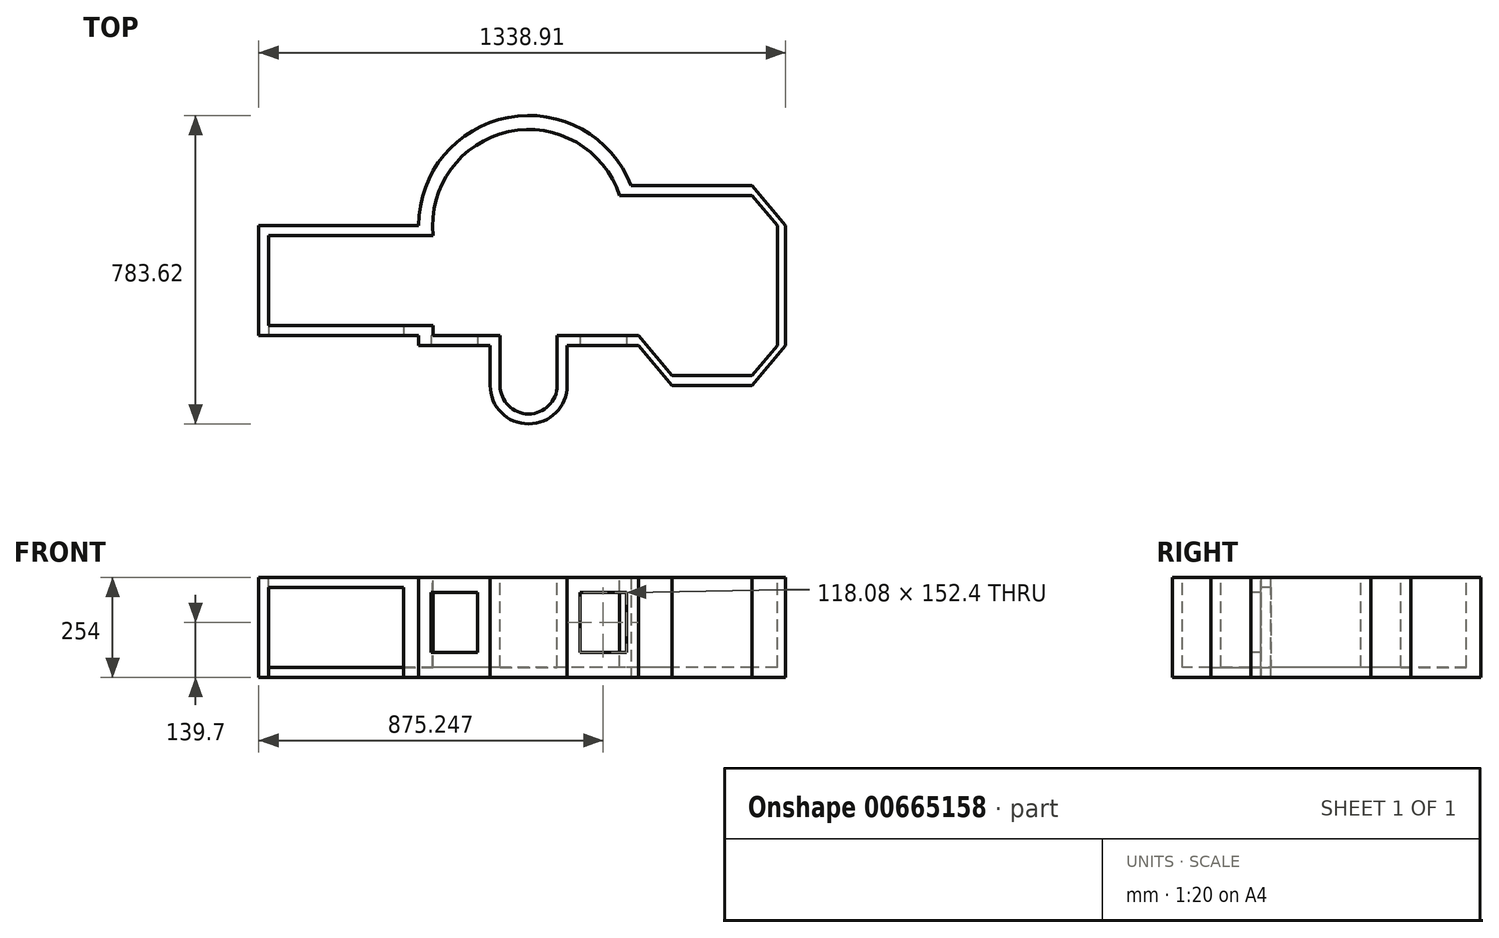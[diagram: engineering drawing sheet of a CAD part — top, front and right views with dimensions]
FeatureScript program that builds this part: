
annotation { "Feature Type Name" : "Feature", "Feature Type Description" : "" }
export const myFeature = defineFeature(function(context is Context, id is Id, definition is map)
    precondition{}
    {
        {
            var Q0;
            Q0=qCreatedBy(makeId("Top.planeOp"),FACE);
            var sketch = newSketch(context, id + "F0", { "sketchPlane" : qUnion([Q0])});
            skLineSegment(sketch, "E0.bottom", {"start": v(279.4, -152.4) * mm, "end": v(97.82, -152.4) * mm});
            skLineSegment(sketch, "E0.right", {"start": v(-279.4, -152.4) * mm, "end": v(-279.4, -127) * mm});
            skPoint(sketch, "E0.middle", {"position": v(0, 0) * mm});
            skLineSegment(sketch, "E1.0", {"start": v(-97.82, -152.4) * mm, "end": v(-97.82, -254) * mm});
            skLineSegment(sketch, "E2.0", {"start": v(97.82, -152.4) * mm, "end": v(97.82, -254) * mm});
            skLineSegment(sketch, "E3", {"start": v(-279.4, 152.4) * mm, "end": v(-685.8, 152.4) * mm});
            skLineSegment(sketch, "E4", {"start": v(-685.8, 152.4) * mm, "end": v(-685.8, -127) * mm});
            skLineSegment(sketch, "E5", {"start": v(-685.8, -127) * mm, "end": v(-279.4, -127) * mm});
            skLineSegment(sketch, "E6", {"start": v(567.85, 254) * mm, "end": v(653.1, 152.4) * mm});
            skLineSegment(sketch, "E7", {"start": v(653.1, 152.4) * mm, "end": v(653.1, -152.4) * mm});
            skLineSegment(sketch, "E8", {"start": v(653.1, -152.4) * mm, "end": v(567.85, -254) * mm});
            skLineSegment(sketch, "E9", {"start": v(567.85, -254) * mm, "end": v(364.65, -254) * mm});
            skLineSegment(sketch, "E10", {"start": v(364.65, -254) * mm, "end": v(279.4, -152.4) * mm});
            skArc(sketch, "E11", {"start": v(-97.82, -254) * mm, "mid": v(0, -351.82) * mm, "end": v(97.82, -254) * mm});
            skLineSegment(sketch, "E12.trimOffspring", {"start": v(-97.82, -152.4) * mm, "end": v(-279.4, -152.4) * mm});
            skArc(sketch, "E13", {"start": v(260.27, 254) * mm, "mid": v(-51.7, 426.98) * mm, "end": v(-279.4, 152.4) * mm});
            skLineSegment(sketch, "E14", {"start": v(567.85, 254) * mm, "end": v(260.27, 254) * mm});
            skSolve(sketch);
        }
        {
            var Q0;
            Q0=makeQuery(id+"F0.imprint","IMPRINT",FACE,{"disambiguationData":[TD([[makeQuery(id+"F0.imprint","IMPRINT",EDGE,{"derivedFrom":sQuery(id+"F0.wireOp",EDGE,"E0.bottom")}),-1.0]])]});
            extrude(context, id + "F1", {"entities" : qUnion([Q0]), "depth" : 254 * mm, "offsetDistance" : 25.4 * mm});
        }
        {
            var Q0;
            Q0=makeQuery(id+"F1.opExtrude","CAP_FACE",FACE,{"disambiguationData":[OSD([sQuery(id+"F0.wireOp",EDGE,"E0.bottom"),sQuery(id+"F0.wireOp",EDGE,"E0.top"),sQuery(id+"F0.wireOp",EDGE,"E0.right"),sQuery(id+"F0.wireOp",EDGE,"E1.0"),sQuery(id+"F0.wireOp",EDGE,"E2.0"),sQuery(id+"F0.wireOp",EDGE,"E3"),sQuery(id+"F0.wireOp",EDGE,"E4"),sQuery(id+"F0.wireOp",EDGE,"E5"),sQuery(id+"F0.wireOp",EDGE,"Ftyo3VZW-W6Cl-7DJd-JTpf-SODImL5dgCJK"),sQuery(id+"F0.wireOp",EDGE,"4KbfmUMY-FonG-mjiz-o9gH-zrDHLoAnOjZW"),sQuery(id+"F0.wireOp",EDGE,"E6"),sQuery(id+"F0.wireOp",EDGE,"E7"),sQuery(id+"F0.wireOp",EDGE,"E8"),sQuery(id+"F0.wireOp",EDGE,"E9"),sQuery(id+"F0.wireOp",EDGE,"E10"),sQuery(id+"F0.wireOp",EDGE,"E11"),sQuery(id+"F0.wireOp",EDGE,"E12.trimOffspring")])],"isStart":false});
            var sketch = newSketch(context, id + "F2", { "sketchPlane" : qUnion([Q0])});
            skLineSegment(sketch, "E15.bottom", {"start": v(242.2, -127) * mm, "end": v(72.42, -127) * mm});
            skLineSegment(sketch, "E15.right", {"start": v(-242.2, -127) * mm, "end": v(-242.2, -101.6) * mm});
            skLineSegment(sketch, "E16", {"start": v(-242.2, 127) * mm, "end": v(-660.4, 127) * mm});
            skLineSegment(sketch, "E17", {"start": v(-660.4, 127) * mm, "end": v(-660.4, -101.6) * mm});
            skLineSegment(sketch, "E18", {"start": v(-660.4, -101.6) * mm, "end": v(-242.2, -101.6) * mm});
            skLineSegment(sketch, "E19", {"start": v(567.85, 228.6) * mm, "end": v(631.8, 152.4) * mm});
            skLineSegment(sketch, "E20", {"start": v(631.8, 152.4) * mm, "end": v(631.8, -152.4) * mm});
            skLineSegment(sketch, "E21", {"start": v(631.8, -152.4) * mm, "end": v(567.85, -228.6) * mm});
            skLineSegment(sketch, "E22", {"start": v(567.85, -228.6) * mm, "end": v(364.65, -228.6) * mm});
            skLineSegment(sketch, "E23", {"start": v(364.65, -228.6) * mm, "end": v(279.4, -127) * mm});
            skLineSegment(sketch, "E24", {"start": v(279.4, -127) * mm, "end": v(242.2, -127) * mm});
            skArc(sketch, "E25", {"start": v(-72.42, -254) * mm, "mid": v(0, -326.42) * mm, "end": v(72.42, -254) * mm});
            skLineSegment(sketch, "E26", {"start": v(-72.42, -254) * mm, "end": v(-72.42, -127) * mm});
            skLineSegment(sketch, "E27", {"start": v(72.42, -254) * mm, "end": v(72.42, -127) * mm});
            skLineSegment(sketch, "E28.trimOffspring", {"start": v(-72.42, -127) * mm, "end": v(-242.2, -127) * mm});
            skArc(sketch, "E29", {"start": v(231.3, 228.6) * mm, "mid": v(-51.1, 390.52) * mm, "end": v(-242.2, 127) * mm});
            skLineSegment(sketch, "E30", {"start": v(567.85, 228.6) * mm, "end": v(231.3, 228.6) * mm});
            skSolve(sketch);
        }
        {
            var Q0;
            Q0=makeQuery(id+"F2.imprint","IMPRINT",FACE,{"disambiguationData":[TD([[makeQuery(id+"F2.imprint","IMPRINT",EDGE,{"derivedFrom":sQuery(id+"F2.wireOp",EDGE,"E15.bottom")}),-1.0]])]});
            extrude(context, id + "F3", {"entities" : qUnion([Q0]), "operationType" : NewBodyOperationType.REMOVE, "oppositeDirection" : true, "depth" : 228.6 * mm, "offsetDistance" : 25.4 * mm});
        }
        {
            var Q0;
            Q0=makeQuery(id+"F1.opExtrude","SWEPT_FACE",FACE,{"disambiguationData":[OSD([sQuery(id+"F0.wireOp",EDGE,"E5")])]});
            var sketch = newSketch(context, id + "F4", { "sketchPlane" : qUnion([Q0])});
            skLineSegment(sketch, "E31", {"start": v(-660.4, 0) * mm, "end": v(-660.4, 228.6) * mm});
            skLineSegment(sketch, "E32", {"start": v(-660.4, 228.6) * mm, "end": v(-317.5, 228.6) * mm});
            skLineSegment(sketch, "E33", {"start": v(-317.5, 228.6) * mm, "end": v(-317.5, 0) * mm});
            skSolve(sketch);
        }
        {
            var Q0;
            Q0=makeQuery(id+"F1.opExtrude","SWEPT_FACE",FACE,{"disambiguationData":[OSD([sQuery(id+"F0.wireOp",EDGE,"E12.trimOffspring")])]});
            var sketch = newSketch(context, id + "F5", { "sketchPlane" : qUnion([Q0])});
            skPoint(sketch, "E34.endSnap0", {"position": v(-188.6, 254) * mm});
            skLineSegment(sketch, "E35.bottom", {"start": v(-247.65, 215.9) * mm, "end": v(-129.57, 215.9) * mm});
            skLineSegment(sketch, "E35.top", {"start": v(-247.65, 63.5) * mm, "end": v(-129.57, 63.5) * mm});
            skLineSegment(sketch, "E35.left", {"start": v(-247.65, 215.9) * mm, "end": v(-247.65, 63.5) * mm});
            skLineSegment(sketch, "E35.right", {"start": v(-129.57, 215.9) * mm, "end": v(-129.57, 63.5) * mm});
            skLineSegment(sketch, "E36.bottom", {"start": v(130.4, 215.9) * mm, "end": v(248.49, 215.9) * mm});
            skLineSegment(sketch, "E36.top", {"start": v(130.4, 63.5) * mm, "end": v(248.49, 63.5) * mm});
            skLineSegment(sketch, "E36.left", {"start": v(130.4, 215.9) * mm, "end": v(130.4, 63.5) * mm});
            skLineSegment(sketch, "E36.right", {"start": v(248.49, 215.9) * mm, "end": v(248.49, 63.5) * mm});
            skSolve(sketch);
        }
        {
            var Q0;
            Q0=makeQuery(id+"F5.imprint","IMPRINT",FACE,{"disambiguationData":[TD([[makeQuery(id+"F5.imprint","IMPRINT",EDGE,{"derivedFrom":sQuery(id+"F5.wireOp",EDGE,"E35.bottom")}),-1.0]])]});
            var Q1;
            Q1=makeQuery(id+"F5.imprint","IMPRINT",FACE,{"disambiguationData":[TD([[makeQuery(id+"F5.imprint","IMPRINT",EDGE,{"derivedFrom":sQuery(id+"F5.wireOp",EDGE,"E36.bottom")}),-1.0]])]});
            var Q2;
            {var subQ0=sQuery(id+"F4.wireOp",EDGE,"E31");Q2=makeQuery(id+"F4.imprint","IMPRINT",FACE,{"disambiguationData":[TD([[makeQuery(id+"F4.imprint","IMPRINT",EDGE,{"derivedFrom":subQ0}),-1.0]])]});}
            extrude(context, id + "F6", {"entities" : qUnion([Q0, Q1, Q2]), "operationType" : NewBodyOperationType.REMOVE, "oppositeDirection" : true, "depth" : 25.4 * mm, "offsetDistance" : 25.4 * mm});
        }
    });
